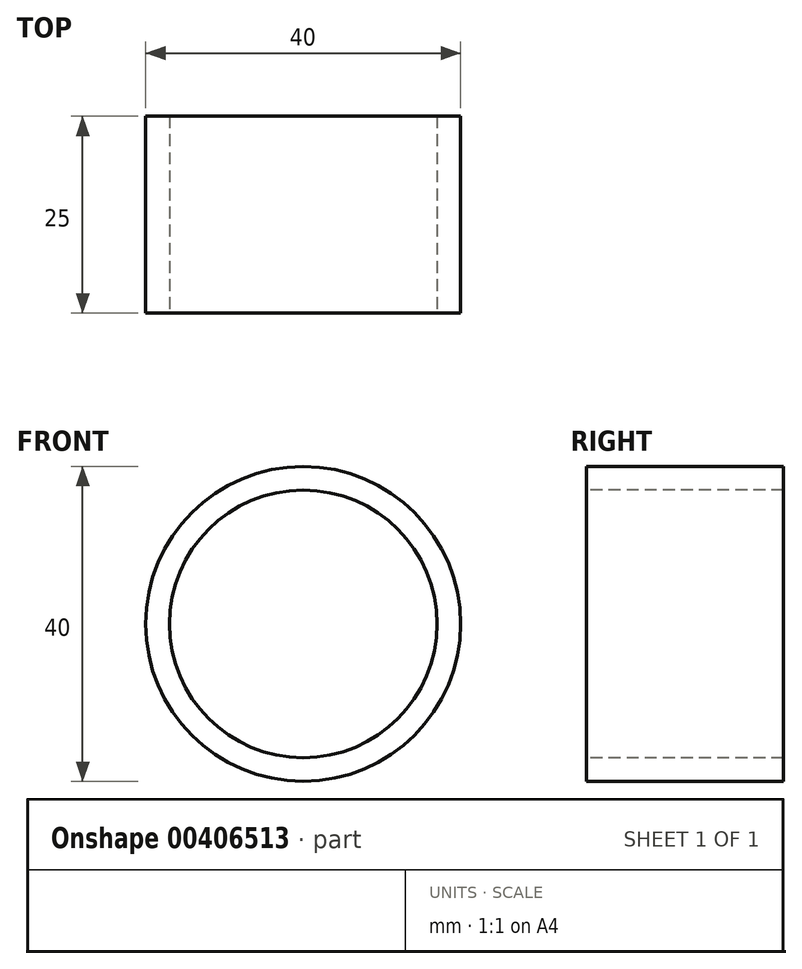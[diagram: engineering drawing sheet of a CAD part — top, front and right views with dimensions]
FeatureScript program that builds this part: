
annotation { "Feature Type Name" : "Feature", "Feature Type Description" : "" }
export const myFeature = defineFeature(function(context is Context, id is Id, definition is map)
    precondition{}
    {
        {
            var Q0;
            Q0=qCreatedBy(makeId("Front.planeOp"),FACE);
            var sketch = newSketch(context, id + "F0", { "sketchPlane" : qUnion([Q0])});
            skLineSegment(sketch, "E0", {"start": v(0, 38.74) * mm, "end": v(0, -44.96) * mm, "construction": true});
            skCircle(sketch, "E1", {"center": v(-31.5, 0) * mm, "radius": 20 * mm});
            skCircle(sketch, "E2.MirrorC", {"center": v(31.5, 0) * mm, "radius": 20 * mm});
            skCircle(sketch, "E3.0", {"center": v(-31.5, 0) * mm, "radius": 17 * mm});
            skCircle(sketch, "E4.0", {"center": v(31.5, 0) * mm, "radius": 17 * mm});
            skFitSpline(sketch, "E5", {"points": [v(-123.25, 11.2) * mm, v(-100.65, 16.98) * mm, v(-84.24, -8.86) * mm, v(-119.03, 2.73) * mm, v(-123.25, 11.2) * mm]});
            skFitSpline(sketch, "E6", {"points": [v(-56.65, 67.42) * mm, v(3.6, 95.68) * mm, v(68.67, 67.04) * mm], "startDerivative": vector(121.15, 85.45) * mm, "endDerivative": vector(129.43, -85.25) * mm});
            skSolve(sketch);
        }
        {
            var Q0;
            Q0=sQuery(id+"F0.wireOp",EDGE,"E3.0");
            var Q1;
            Q1=sQuery(id+"F0.wireOp",EDGE,"E1");
            extrude(context, id + "F1", {"bodyType" : ToolBodyType.SURFACE, "surfaceEntities" : qUnion([Q0, Q1]), "depth" : 25 * mm});
        }
    });
